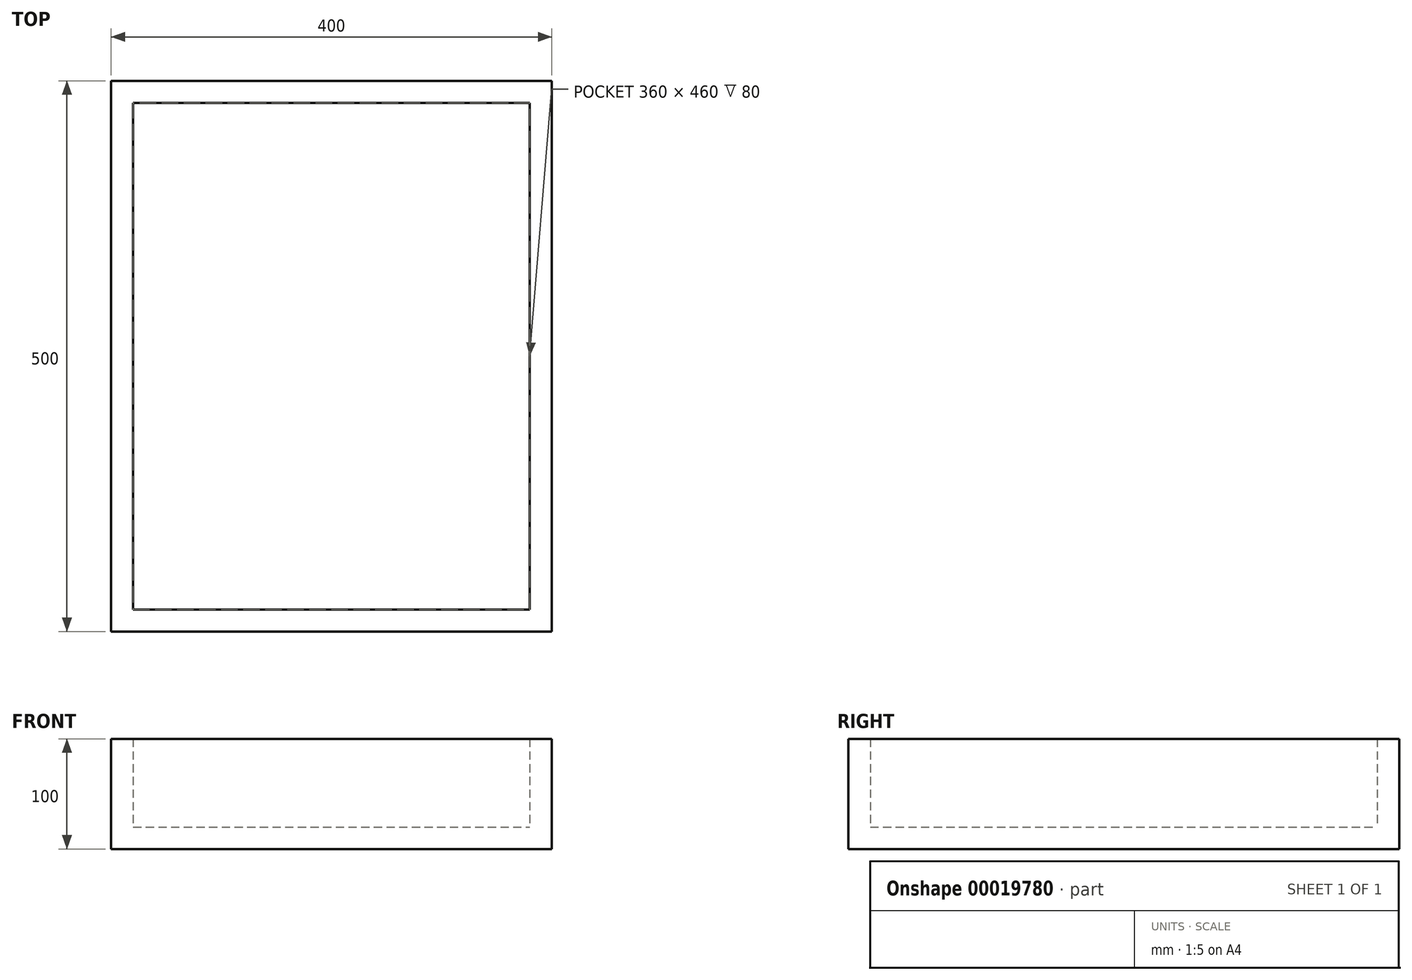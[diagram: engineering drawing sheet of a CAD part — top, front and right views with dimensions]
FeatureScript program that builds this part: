
annotation { "Feature Type Name" : "Feature", "Feature Type Description" : "" }
export const myFeature = defineFeature(function(context is Context, id is Id, definition is map)
    precondition{}
    {
        {
            var Q0;
            Q0=qCreatedBy(makeId("Top.planeOp"),FACE);
            var sketch = newSketch(context, id + "F0", { "sketchPlane" : qUnion([Q0])});
            skLineSegment(sketch, "E0.bottom", {"start": v(0, 0) * mm, "end": v(400, 0) * mm});
            skLineSegment(sketch, "E0.top", {"start": v(0, 500) * mm, "end": v(400, 500) * mm});
            skLineSegment(sketch, "E0.left", {"start": v(0, 0) * mm, "end": v(0, 500) * mm});
            skLineSegment(sketch, "E0.right", {"start": v(400, 0) * mm, "end": v(400, 500) * mm});
            skSolve(sketch);
        }
        {
            var Q0;
            Q0 = qSketchRegion(id + "F0", true);
            extrude(context, id + "F1", {"entities" : qUnion([Q0]), "depth" : 100 * mm});
        }
        {
            var Q0;
            Q0=makeQuery(id+"F1.opExtrude","CAP_FACE",FACE,{"disambiguationData":[OSD([sQuery(id+"F0.wireOp",EDGE,"E0.bottom"),sQuery(id+"F0.wireOp",EDGE,"E0.top"),sQuery(id+"F0.wireOp",EDGE,"E0.left"),sQuery(id+"F0.wireOp",EDGE,"E0.right")])],"isStart":false});
            shell(context, id + "F2", {"entities" : qUnion([Q0]), "thickness" : 20 * mm});
        }
    });
